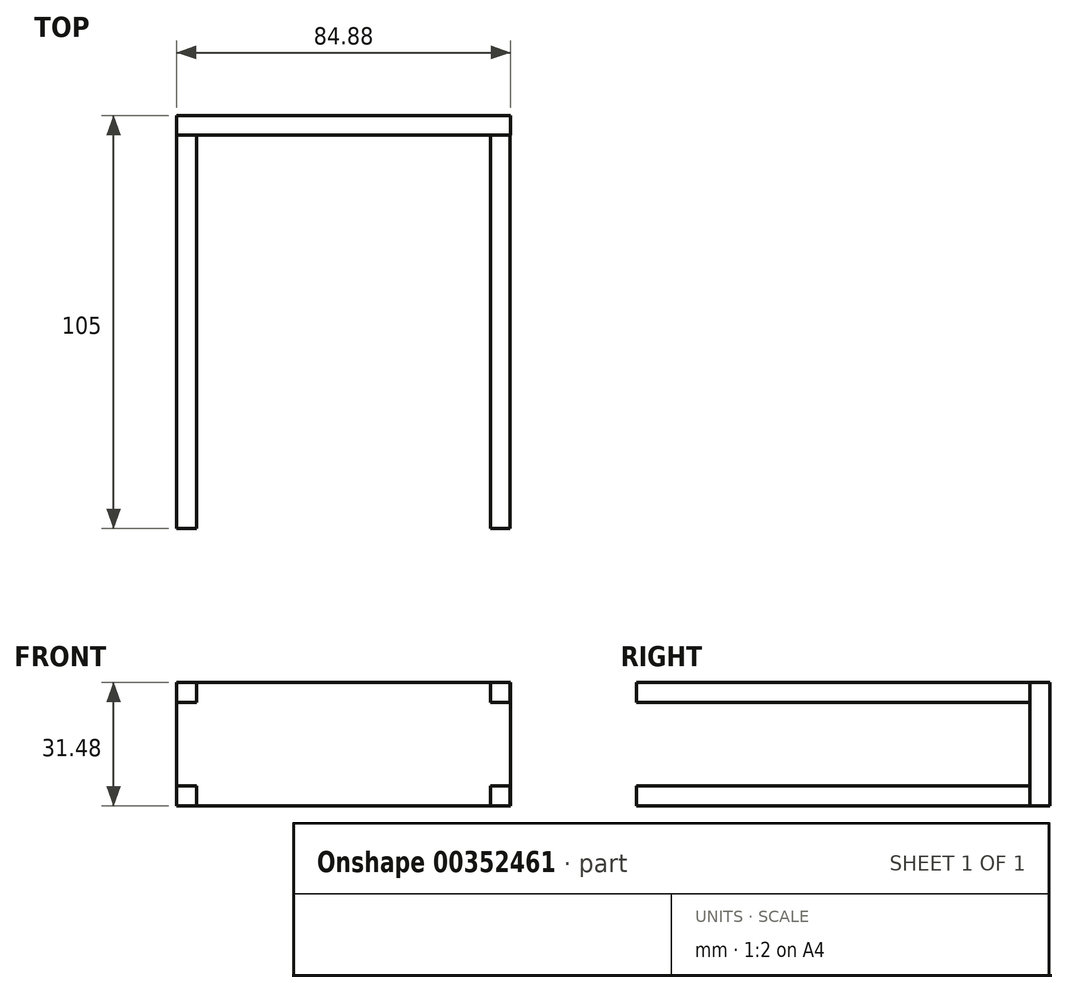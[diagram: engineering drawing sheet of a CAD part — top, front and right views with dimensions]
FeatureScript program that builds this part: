
annotation { "Feature Type Name" : "Feature", "Feature Type Description" : "" }
export const myFeature = defineFeature(function(context is Context, id is Id, definition is map)
    precondition{}
    {
        {
            var Q0;
            Q0=qCreatedBy(makeId("Front.planeOp"),FACE);
            var sketch = newSketch(context, id + "F0", { "sketchPlane" : qUnion([Q0])});
            skLineSegment(sketch, "E0.bottom", {"start": v(-42.44, 15.74) * mm, "end": v(42.44, 15.74) * mm});
            skLineSegment(sketch, "E0.top", {"start": v(-42.44, -15.74) * mm, "end": v(42.44, -15.74) * mm});
            skLineSegment(sketch, "E0.left", {"start": v(-42.44, 15.74) * mm, "end": v(-42.44, -15.74) * mm});
            skLineSegment(sketch, "E0.right", {"start": v(42.44, 15.74) * mm, "end": v(42.44, -15.74) * mm});
            skPoint(sketch, "E0.middle", {"position": v(0, 0) * mm});
            skSolve(sketch);
        }
        {
            var Q0;
            Q0 = qSketchRegion(id + "F0", true);
            extrude(context, id + "F1", {"entities" : qUnion([Q0]), "depth" : 5 * mm});
        }
        {
            var Q0;
            Q0=qCreatedBy(makeId("Front.planeOp"),FACE);
            var sketch = newSketch(context, id + "F2", { "sketchPlane" : qUnion([Q0])});
            skLineSegment(sketch, "E1.bottom", {"start": v(-42.36, 15.65) * mm, "end": v(-37.36, 15.65) * mm});
            skLineSegment(sketch, "E1.top", {"start": v(-42.36, 10.65) * mm, "end": v(-37.36, 10.65) * mm});
            skLineSegment(sketch, "E1.left", {"start": v(-42.36, 15.65) * mm, "end": v(-42.36, 10.65) * mm});
            skLineSegment(sketch, "E1.right", {"start": v(-37.36, 15.65) * mm, "end": v(-37.36, 10.65) * mm});
            skLineSegment(sketch, "E2.MirrorCS", {"start": v(42.36, 15.65) * mm, "end": v(37.36, 15.65) * mm});
            skLineSegment(sketch, "E3.MirrorCS", {"start": v(42.36, 10.65) * mm, "end": v(37.36, 10.65) * mm});
            skLineSegment(sketch, "E4.MirrorCS", {"start": v(42.36, 15.65) * mm, "end": v(42.36, 10.65) * mm});
            skLineSegment(sketch, "E5.MirrorCS", {"start": v(37.36, 15.65) * mm, "end": v(37.36, 10.65) * mm});
            skLineSegment(sketch, "E6.MirrorCS", {"start": v(42.36, -15.65) * mm, "end": v(42.36, -10.65) * mm});
            skLineSegment(sketch, "E7.MirrorCS", {"start": v(42.36, -10.65) * mm, "end": v(37.36, -10.65) * mm});
            skLineSegment(sketch, "E8.MirrorCS", {"start": v(42.36, -15.65) * mm, "end": v(37.36, -15.65) * mm});
            skLineSegment(sketch, "E9.MirrorCS", {"start": v(-37.36, -15.65) * mm, "end": v(-37.36, -10.65) * mm});
            skLineSegment(sketch, "E10.MirrorCS", {"start": v(-42.36, -15.65) * mm, "end": v(-42.36, -10.65) * mm});
            skLineSegment(sketch, "E11.MirrorCS", {"start": v(-42.36, -10.65) * mm, "end": v(-37.36, -10.65) * mm});
            skLineSegment(sketch, "E12.MirrorCS", {"start": v(-42.36, -15.65) * mm, "end": v(-37.36, -15.65) * mm});
            skLineSegment(sketch, "E13.MirrorCS", {"start": v(37.36, -15.65) * mm, "end": v(37.36, -10.65) * mm});
            skSolve(sketch);
        }
        {
            var Q0;
            Q0 = qSketchRegion(id + "F2", true);
            extrude(context, id + "F3", {"entities" : qUnion([Q0]), "operationType" : NewBodyOperationType.ADD, "depth" : 105 * mm});
        }
    });
